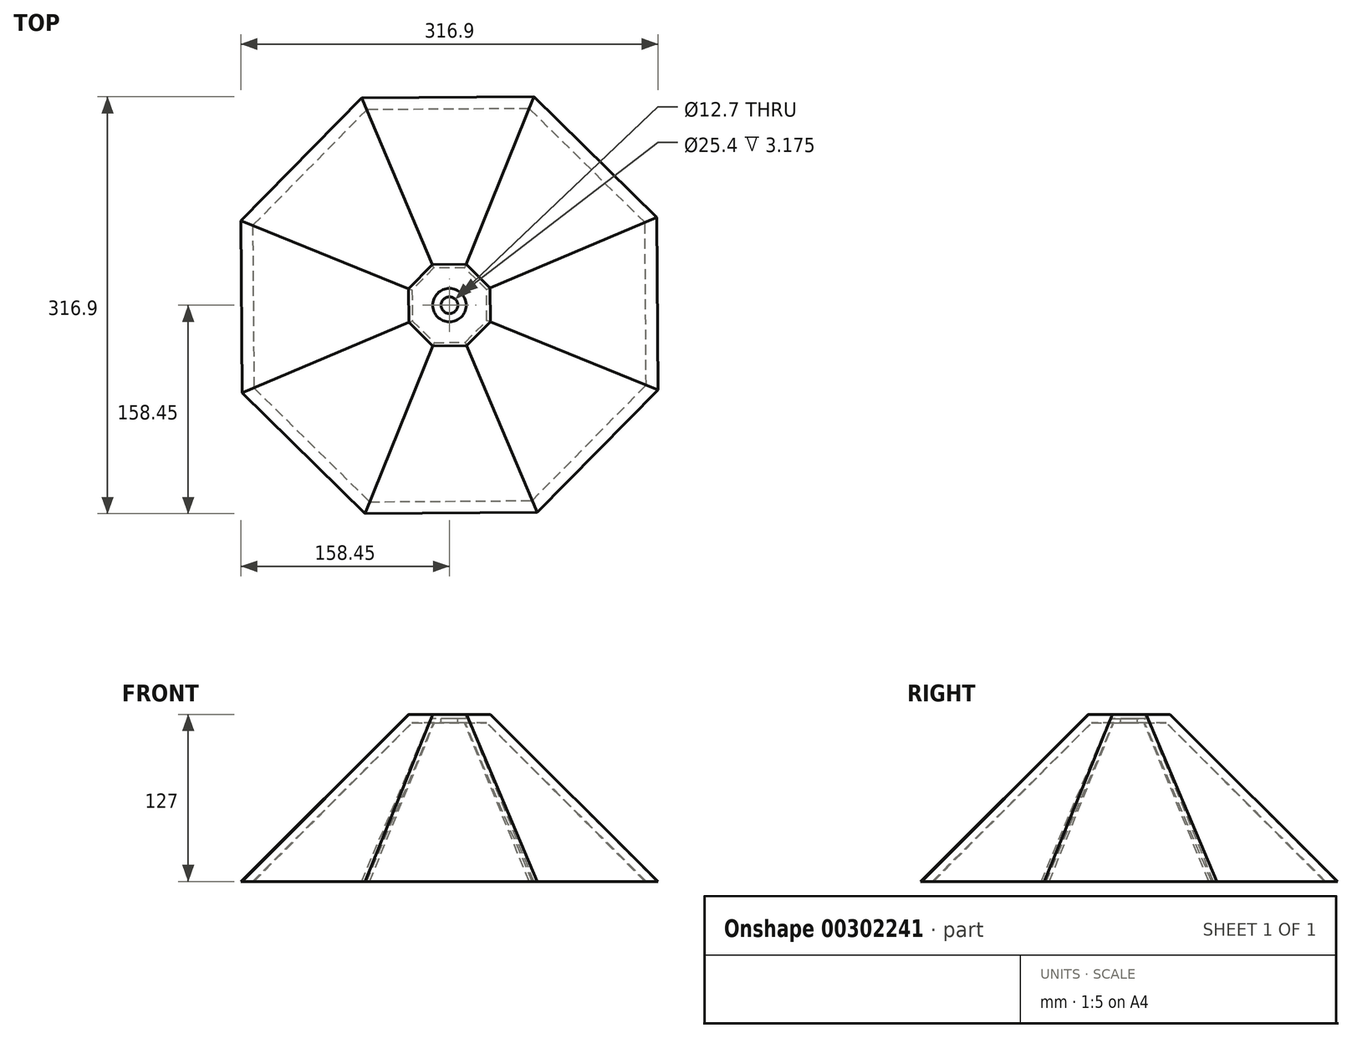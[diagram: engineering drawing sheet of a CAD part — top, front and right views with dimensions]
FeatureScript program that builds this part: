
annotation { "Feature Type Name" : "Feature", "Feature Type Description" : "" }
export const myFeature = defineFeature(function(context is Context, id is Id, definition is map)
    precondition{}
    {
        {
            var Q0;
            Q0=qCreatedBy(makeId("Top.planeOp"),FACE);
            var sketch = newSketch(context, id + "F0", { "sketchPlane" : qUnion([Q0])});
            skCircle(sketch, "E0.cCircle", {"center": v(0, 0) * mm, "radius": 30.96 * mm, "construction": true});
            skLineSegment(sketch, "E0.0", {"start": v(-31.05, 12.59) * mm, "end": v(-13.06, 30.86) * mm});
            skLineSegment(sketch, "E0.1", {"start": v(-13.06, 30.86) * mm, "end": v(12.59, 31.05) * mm});
            skLineSegment(sketch, "E0.2", {"start": v(12.59, 31.05) * mm, "end": v(30.86, 13.06) * mm});
            skLineSegment(sketch, "E0.3", {"start": v(30.86, 13.06) * mm, "end": v(31.05, -12.59) * mm});
            skLineSegment(sketch, "E0.4", {"start": v(31.05, -12.59) * mm, "end": v(13.06, -30.86) * mm});
            skLineSegment(sketch, "E0.5", {"start": v(13.06, -30.86) * mm, "end": v(-12.59, -31.05) * mm});
            skLineSegment(sketch, "E0.6", {"start": v(-12.59, -31.05) * mm, "end": v(-30.86, -13.06) * mm});
            skLineSegment(sketch, "E0.7", {"start": v(-30.86, -13.06) * mm, "end": v(-31.05, 12.59) * mm});
            skPoint(sketch, "E0.0.midPoint", {"position": v(-22.05, 21.72) * mm});
            skSolve(sketch);
        }
        {
            var Q0;
            Q0 = qSketchRegion(id + "F0", true);
            extrude(context, id + "F1", {"entities" : qUnion([Q0]), "oppositeDirection" : true, "depth" : 127 * mm, "hasDraft" : true, "draftAngle" : 45 * degree});
        }
        {
            var Q0;
            Q0=makeQuery(id+"F1.opExtrude","CAP_FACE",FACE,{"disambiguationData":[OSD([sQuery(id+"F0.wireOp",EDGE,"E0.0"),sQuery(id+"F0.wireOp",EDGE,"E0.1"),sQuery(id+"F0.wireOp",EDGE,"E0.2"),sQuery(id+"F0.wireOp",EDGE,"E0.3"),sQuery(id+"F0.wireOp",EDGE,"E0.4"),sQuery(id+"F0.wireOp",EDGE,"E0.5"),sQuery(id+"F0.wireOp",EDGE,"E0.6"),sQuery(id+"F0.wireOp",EDGE,"E0.7")])],"isStart":false});
            shell(context, id + "F2", {"entities" : qUnion([Q0]), "thickness" : 6.35 * mm});
        }
        {
            var Q0;
            Q0=makeQuery(id+"F1.opExtrude","CAP_FACE",FACE,{"disambiguationData":[OSD([sQuery(id+"F0.wireOp",EDGE,"E0.0"),sQuery(id+"F0.wireOp",EDGE,"E0.1"),sQuery(id+"F0.wireOp",EDGE,"E0.2"),sQuery(id+"F0.wireOp",EDGE,"E0.3"),sQuery(id+"F0.wireOp",EDGE,"E0.4"),sQuery(id+"F0.wireOp",EDGE,"E0.5"),sQuery(id+"F0.wireOp",EDGE,"E0.6"),sQuery(id+"F0.wireOp",EDGE,"E0.7")])],"isStart":true});
            var sketch = newSketch(context, id + "F3", { "sketchPlane" : qUnion([Q0])});
            skPoint(sketch, "E1", {"position": v(0, 0) * mm});
            skLineSegment(sketch, "E2", {"start": v(-30.96, 0) * mm, "end": v(0, 0) * mm});
            skSolve(sketch);
        }
        {
            var Q0;
            Q0=sQuery(id+"F3.wireOp",VERTEX,"E1");
            var Q1;
            Q1=makeQuery(id+"F1.opExtrude","SWEPT_BODY",BODY,{"disambiguationData":[OSD([sQuery(id+"F0.wireOp",EDGE,"E0.0"),sQuery(id+"F0.wireOp",EDGE,"E0.1"),sQuery(id+"F0.wireOp",EDGE,"E0.2"),sQuery(id+"F0.wireOp",EDGE,"E0.3"),sQuery(id+"F0.wireOp",EDGE,"E0.4"),sQuery(id+"F0.wireOp",EDGE,"E0.5"),sQuery(id+"F0.wireOp",EDGE,"E0.6"),sQuery(id+"F0.wireOp",EDGE,"E0.7")])]});
            hole(context, id + "F4", {"style" : HoleStyle.C_BORE, "endStyle" : HoleEndStyle.THROUGH, "holeDiameter" : 12.7 * mm, "cBoreDiameter" : 25.4 * mm, "cBoreDepth" : 3.17 * mm, "tappedDepth" : 12.7 * mm, "tapClearance" : 3, "locations" : qUnion([Q0]), "scope" : qUnion([Q1])});
        }
    });
